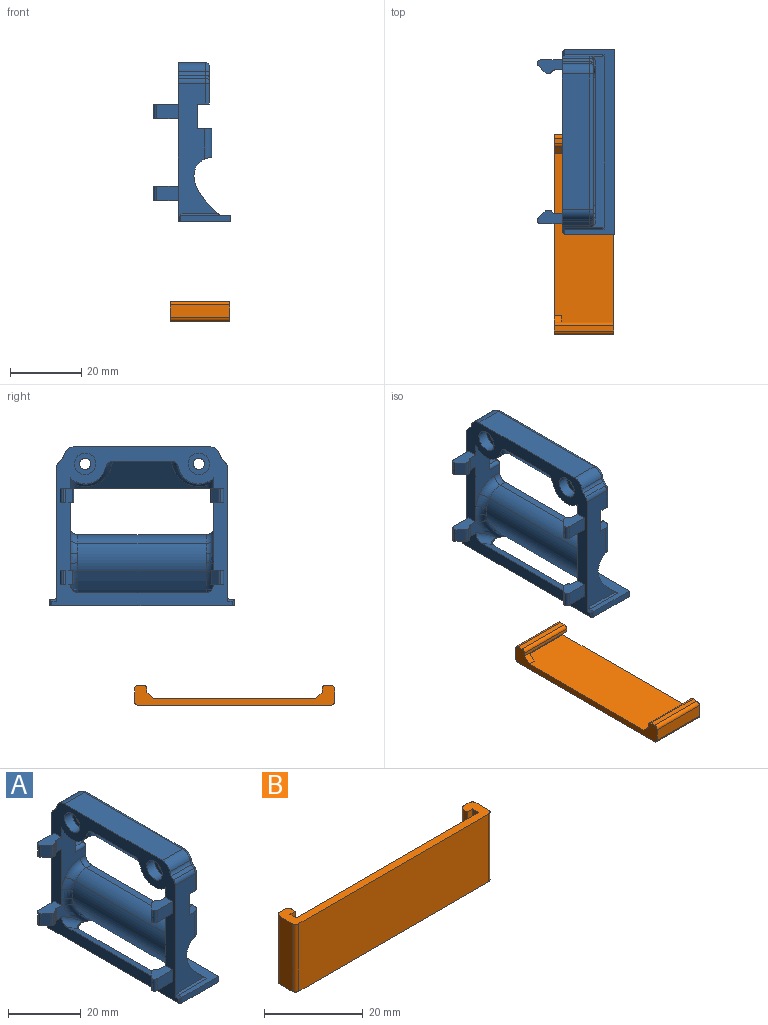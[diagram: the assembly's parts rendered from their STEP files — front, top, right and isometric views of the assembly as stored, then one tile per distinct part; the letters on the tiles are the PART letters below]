
ASSEMBLY  parts=2 mates=1
PART A: 131 faces, bbox 22.5x52.8x50.8 mm
  f0: plane 8.17x6.43mm, normal (0,1,0), area 16.5mm2, adj f30,f65,f66,f67,f90,f91,f120
  f1: plane 8.17x6.43mm, normal (0,-1,0), area 16.5mm2, adj f30,f72,f73,f74,f87,f89,f122
  f2: plane 21.12x11.5mm, normal (0,-1,0), area 100.7mm2, adj f8,f23,f28,f30,f59,f68,f69,f70
  f3: plane 21.12x11.5mm, normal (0,1,0), area 100.7mm2, adj f7,f23,f29,f30,f58,f61,f62,f63
  f4: cylinder r=1.6mm len=5.8mm, axis (-1,0,0), area 58.3mm2, adj f12,f34
  f5: cylinder r=1.6mm len=5.8mm, axis (-1,0,0), area 58.3mm2, adj f12,f36
  f6: plane 14.2x1.87mm, normal (0,-1,0), area 26.6mm2, adj f9,f17,f18,f83
  f7: plane 8.04x4.12mm, normal (1,0,0), area 26.9mm2, adj f3,f11,f22,f38,f58,f127
  f8: plane 8.04x4.12mm, normal (1,0,0), area 26.9mm2, adj f2,f11,f20,f37,f59,f129
  f9: plane 52.1x14.8mm, normal (0,0,-1), area 483.7mm2, adj f6,f16,f17,f30,f75,f76,f77,f78
  f10: cylinder r=28.2mm len=49.1mm, axis (0,1,0), area 397.8mm2, adj f18,f24,f37,f38,f85,f86
  f11: plane 48.51x3.71mm, normal (0,0,-1), area 106.9mm2, adj f7,f8,f12,f25,f37,f38,f47,f53
  f12: plane 46.1x10.6mm, normal (1,0,0), area 457.4mm2, adj f4,f5,f11,f47,f48,f49,f50,f51
  f13: plane 38.1x7.8mm, normal (0,0,1), area 297.2mm2, adj f26,f27,f30,f52
  f14: cylinder r=30mm len=36.1mm, axis (0,1,0), area 454.7mm2, adj f31,f67,f74,f78
  f15: plane 36.1x4.52mm, normal (0.53,0,0.85), area 192.5mm2, adj f30,f66,f73,f77
  f16: plane 14.2x1.87mm, normal (0,1,0), area 26.6mm2, adj f9,f17,f18,f81
  f17: plane 52.1x1.87mm, normal (1,0,0), area 97.6mm2, adj f6,f9,f16,f18
  f18: plane 52.1x14.2mm, normal (0,0,1), area 190.5mm2, adj f6,f10,f16,f17,f82,f84,f85,f86
  f19: plane 45.02x0.05mm, normal (0,0,-1), area 2.4mm2, adj f23,f32,f43,f44
  f20: plane 4x2.8mm, normal (0,0,1), area 10.3mm2, adj f8,f23,f37,f44,f59
  f21: plane 36.1x1.99mm, normal (0,0,1), area 72mm2, adj f23,f60,f61,f68
  f22: plane 4x2.8mm, normal (0,0,1), area 10.3mm2, adj f7,f23,f38,f43,f58
  f23: plane 44.1x8.12mm, normal (1,0,0), area 108.4mm2, adj f2,f3,f19,f20,f21,f22,f43,f44
  f24: cylinder r=10mm len=48.1mm, axis (0,1,0), area 243.1mm2, adj f10,f32,f37,f38
  f25: plane 36.5x7.58mm, normal (-0.74,0,-0.67), area 216.3mm2, adj f11,f30,f127,f128,f129,f130
  f26: cylinder r=3mm len=7.8mm, axis (-1,0,0), area 32.5mm2, adj f13,f30,f46,f54
  f27: cylinder r=3mm len=7.8mm, axis (1,0,0), area 32.5mm2, adj f13,f30,f45,f51
  f28: cylinder r=5.69mm len=9.7mm, axis (1,0,0), area 42.8mm2, adj f2,f30,f129,f130
  f29: cylinder r=5.69mm len=9.7mm, axis (1,0,0), area 42.8mm2, adj f3,f30,f127,f128
  f30: plane 51.59x45.49mm, normal (-1,0,0), area 651.8mm2, adj f0,f1,f2,f3,f9,f13,f15,f25
  f31: cylinder r=8mm len=36.1mm, axis (0,-1,0), area 302.4mm2, adj f14,f60,f63,f64,f65,f70,f71,f72
  f32: cylinder r=5mm len=48.1mm, axis (0,1,0), area 398mm2, adj f19,f24,f37,f38,f43,f44
  f33: cylinder r=3mm len=6mm, axis (-1,0,0), area 56.5mm2, adj f30,f34
  f34: plane 6x6mm, normal (-1,0,0), area 20.2mm2, adj f4,f33
  f35: cylinder r=3mm len=6mm, axis (-1,0,0), area 56.5mm2, adj f30,f36
  f36: plane 6x6mm, normal (-1,0,0), area 20.2mm2, adj f5,f35
  f37: plane 37.7x11.18mm, normal (0,1,0), area 245.2mm2, adj f8,f10,f11,f20,f24,f30,f32,f41
  f38: plane 37.7x11.18mm, normal (0,-1,0), area 245.2mm2, adj f7,f10,f11,f22,f24,f30,f32,f42
  f39: plane 7.8x0.91mm, normal (0,-0.71,0.71), area 10.1mm2, adj f30,f42,f45,f49
  f40: plane 7.8x0.91mm, normal (0,0.71,0.71), area 10.1mm2, adj f30,f41,f46,f57
  f41: cylinder r=2mm len=7.8mm, axis (1,0,0), area 12.3mm2, adj f30,f37,f40,f55
  f42: cylinder r=2mm len=7.8mm, axis (-1,0,0), area 12.3mm2, adj f30,f38,f39,f48
  f43: cylinder r=2mm len=8.51mm, axis (0,0,-1), area 26mm2, adj f19,f22,f23,f32,f38
  f44: cylinder r=2mm len=8.51mm, axis (0,0,-1), area 26mm2, adj f19,f20,f23,f32,f37
  f45: cylinder r=2mm len=7.8mm, axis (1,0,0), area 9.4mm2, adj f27,f30,f39,f50
  f46: cylinder r=2mm len=7.8mm, axis (-1,0,0), area 9.4mm2, adj f26,f30,f40,f56
  f47: cylinder r=1mm len=5.77mm, axis (0,0,-1), area 9.1mm2, adj f11,f12,f38,f48
  f48: torus R=1mm, axis (1,0,0), area 2mm2, adj f12,f42,f47,f49
  f49: cylinder r=1mm len=1.62mm, axis (0,-0.71,-0.71), area 2mm2, adj f12,f39,f48,f50
  f50: torus R=3mm, axis (1,0,0), area 2.2mm2, adj f12,f45,f49,f51
  f51: torus R=2mm, axis (1,0,0), area 5.7mm2, adj f12,f27,f50,f52
  f52: cylinder r=1mm len=38.1mm, axis (0,1,0), area 59.8mm2, adj f12,f13,f51,f54
  f53: cylinder r=1mm len=5.77mm, axis (0,0,-1), area 9.1mm2, adj f11,f12,f37,f55
  f54: torus R=2mm, axis (1,0,0), area 5.7mm2, adj f12,f26,f52,f56
  f55: torus R=1mm, axis (1,0,0), area 2mm2, adj f12,f41,f53,f57
  f56: torus R=3mm, axis (1,0,0), area 2.2mm2, adj f12,f46,f54,f57
  f57: cylinder r=1mm len=1.62mm, axis (0,-0.71,0.71), area 2mm2, adj f12,f40,f55,f56
  f58: cylinder r=1mm len=4mm, axis (1,0,0), area 6.3mm2, adj f3,f7,f22,f23
  f59: cylinder r=1mm len=4mm, axis (-1,0,0), area 6.3mm2, adj f2,f8,f20,f23
  f60: cylinder r=5mm len=36.1mm, axis (0,-1,0), area 183.9mm2, adj f21,f31,f62,f69
  f61: cylinder r=2.2mm len=2.2mm, axis (-1,0,0), area 6.9mm2, adj f3,f21,f23,f62
  f62: torus R=7.2mm, axis (0,-1,0), area 20.4mm2, adj f3,f60,f61,f63
  f63: torus R=10.2mm, axis (0,-1,0), area 11.8mm2, adj f3,f31,f62,f64
  f64: bspline ~4.73x2.36mm, area 9.7mm2, adj f30,f31,f63,f65
  f65: torus R=10.2mm, axis (0,-1,0), area 10mm2, adj f0,f31,f64,f67
  f66: cylinder r=2.2mm len=9.52mm, axis (-0.85,0,0.53), area 25.8mm2, adj f0,f15,f30,f67,f75
  f67: torus R=32.2mm, axis (0,-1,0), area 39.1mm2, adj f0,f14,f65,f66,f75,f76
  f68: cylinder r=2.2mm len=2.2mm, axis (1,0,0), area 6.9mm2, adj f2,f21,f23,f69
  f69: torus R=7.2mm, axis (0,-1,0), area 20.4mm2, adj f2,f60,f68,f70
  f70: torus R=10.2mm, axis (0,-1,0), area 11.8mm2, adj f2,f31,f69,f71
  f71: bspline ~4.73x2.36mm, area 9.7mm2, adj f30,f31,f70,f72
  f72: torus R=10.2mm, axis (0,-1,0), area 10mm2, adj f1,f31,f71,f74
  f73: cylinder r=2.2mm len=9.52mm, axis (0.85,0,-0.53), area 25.8mm2, adj f1,f15,f30,f74,f79
  f74: torus R=32.2mm, axis (0,-1,0), area 39.1mm2, adj f1,f14,f72,f73,f79,f80
  f75: bspline ~4.67x2.76mm, area 5mm2, adj f9,f66,f67,f76,f77
  f76: bspline ~3.88x2.85mm, area 2.1mm2, adj f9,f67,f75,f78
  f77: cylinder r=0.5mm len=36.1mm, axis (0,1,0), area 46.6mm2, adj f9,f15,f75,f79
  f78: cylinder r=0.5mm len=36.1mm, axis (0,1,0), area 11.8mm2, adj f9,f14,f76,f80
  f79: bspline ~4.67x3.16mm, area 5mm2, adj f9,f73,f74,f77,f80
  f80: bspline ~3.88x2.85mm, area 2.1mm2, adj f9,f74,f78,f79
  f81: plane 1.87x0.6mm, normal (-0.71,0.71,0), area 1.3mm2, adj f9,f16,f30,f82
  f82: plane 2x1.1mm, normal (-0.71,0,0.71), area 1.6mm2, adj f18,f30,f37,f81,f86
  f83: plane 1.87x0.6mm, normal (-0.71,-0.71,0), area 1.3mm2, adj f6,f9,f30,f84
  f84: plane 2x1.1mm, normal (-0.71,0,0.71), area 1.6mm2, adj f18,f30,f38,f83,f85
  f85: plane 11.19x0.5mm, normal (0,-0.71,0.71), area 7.5mm2, adj f10,f18,f38,f84
  f86: plane 11.19x0.5mm, normal (0,0.71,0.71), area 7.5mm2, adj f10,f18,f37,f82
  f87: plane 7x3.8mm, normal (0,0,1), area 20.4mm2, adj f1,f30,f88,f99,f106,f107,f108,f109
  f88: plane 6x4mm, normal (0,1,0), area 24mm2, adj f30,f87,f89,f107
  f89: plane 7x3.8mm, normal (0,0,-1), area 20.4mm2, adj f1,f30,f88,f99,f106,f107,f108,f109
  f90: plane 7x3.8mm, normal (0,0,1), area 20.4mm2, adj f0,f30,f92,f101,f104,f113,f114,f115
  f91: plane 7x3.8mm, normal (0,0,-1), area 20.4mm2, adj f0,f30,f92,f101,f104,f113,f114,f115
  f92: plane 6x4mm, normal (0,-1,0), area 24mm2, adj f30,f90,f91,f114
  f93: plane 7x3.8mm, normal (0,0,1), area 20.4mm2, adj f2,f30,f94,f100,f105,f110,f111,f112
  f94: plane 6x4mm, normal (0,1,0), area 24mm2, adj f30,f93,f95,f110
  f95: plane 7x3.8mm, normal (0,0,-1), area 20.4mm2, adj f2,f30,f94,f100,f105,f110,f111,f112
  f96: plane 6x4mm, normal (0,-1,0), area 24mm2, adj f30,f97,f98,f117
  f97: plane 7x3.8mm, normal (0,0,1), area 20.4mm2, adj f3,f30,f96,f102,f103,f116,f117,f118
  f98: plane 7x3.8mm, normal (0,0,-1), area 20.4mm2, adj f3,f30,f96,f102,f103,f116,f117,f118
  f99: plane 4x0.35mm, normal (0,-1,0), area 1.4mm2, adj f87,f89,f109,f126
  f100: plane 4x0.35mm, normal (0,-1,0), area 1.4mm2, adj f93,f95,f112,f125
  f101: plane 4x0.35mm, normal (0,1,0), area 1.4mm2, adj f90,f91,f113,f124
  f102: plane 4x0.35mm, normal (0,1,0), area 1.4mm2, adj f97,f98,f116,f123
  f103: plane 4x1.91mm, normal (-0.71,0.71,0), area 10.8mm2, adj f97,f98,f116,f118
  f104: plane 4x1.91mm, normal (-0.71,0.71,0), area 10.8mm2, adj f90,f91,f113,f115
  f105: plane 4x1.91mm, normal (-0.71,-0.71,0), area 10.8mm2, adj f93,f95,f111,f112
  f106: plane 4x1.91mm, normal (-0.71,-0.71,0), area 10.8mm2, adj f87,f89,f108,f109
  f107: cylinder r=1mm len=4mm, axis (0,0,1), area 6.1mm2, adj f87,f88,f89,f108
  f108: cylinder r=1mm len=4mm, axis (0,0,-1), area 2.9mm2, adj f87,f89,f106,f107
  f109: cylinder r=1mm len=4mm, axis (0,0,1), area 3.1mm2, adj f87,f89,f99,f106
  f110: cylinder r=1mm len=4mm, axis (0,0,1), area 6.1mm2, adj f93,f94,f95,f111
  f111: cylinder r=1mm len=4mm, axis (0,0,-1), area 2.9mm2, adj f93,f95,f105,f110
  f112: cylinder r=1mm len=4mm, axis (0,0,1), area 3.1mm2, adj f93,f95,f100,f105
  f113: cylinder r=1mm len=4mm, axis (0,0,-1), area 3.1mm2, adj f90,f91,f101,f104
  f114: cylinder r=1mm len=4mm, axis (0,0,-1), area 6.1mm2, adj f90,f91,f92,f115
  f115: cylinder r=1mm len=4mm, axis (0,0,1), area 2.9mm2, adj f90,f91,f104,f114
  f116: cylinder r=1mm len=4mm, axis (0,0,-1), area 3.1mm2, adj f97,f98,f102,f103
  f117: cylinder r=1mm len=4mm, axis (0,0,-1), area 6.1mm2, adj f96,f97,f98,f118
  f118: cylinder r=1mm len=4mm, axis (0,0,1), area 2.9mm2, adj f97,f98,f103,f117
  f119: cylinder r=1mm len=4mm, axis (0,0,1), area 4.2mm2, adj f3,f97,f98,f123
  f120: cylinder r=1mm len=4mm, axis (0,0,1), area 4.2mm2, adj f0,f90,f91,f124
  f121: cylinder r=1mm len=4mm, axis (0,0,1), area 4.2mm2, adj f2,f93,f95,f125
  f122: cylinder r=1mm len=4mm, axis (0,0,1), area 4.2mm2, adj f1,f87,f89,f126
  f123: cylinder r=1mm len=4mm, axis (0,0,1), area 4.2mm2, adj f97,f98,f102,f119
  f124: cylinder r=1mm len=4mm, axis (0,0,1), area 4.2mm2, adj f90,f91,f101,f120
  f125: cylinder r=1mm len=4mm, axis (0,0,1), area 4.2mm2, adj f93,f95,f100,f121
  f126: cylinder r=1mm len=4mm, axis (0,0,1), area 4.2mm2, adj f87,f89,f99,f122
  f127: cylinder r=2mm len=5.88mm, axis (0.67,0,-0.74), area 10.1mm2, adj f3,f7,f11,f25,f29,f128
  f128: bspline ~13.09x7.9mm, area 30.7mm2, adj f25,f29,f30,f127
  f129: cylinder r=2mm len=5.88mm, axis (0.67,0,-0.74), area 10.1mm2, adj f2,f8,f11,f25,f28,f130
  f130: bspline ~13.09x7.9mm, area 30.7mm2, adj f25,f28,f30,f129
PART B: 24 faces, bbox 56.3x5.6x16.8 mm
  f0: plane 56.3x5.6mm, normal (0,0,1), area 121.3mm2, adj f2,f3,f5,f6,f7,f8,f9,f10
  f1: plane 56.3x5.6mm, normal (0,0,-1), area 129.9mm2, adj f2,f5,f6,f7,f9,f13,f14,f15
  f2: plane 16.8x1.5mm, normal (0,1,0), area 25.2mm2, adj f0,f1,f20,f23
  f3: plane 14.8x1.5mm, normal (0,-1,0), area 22.2mm2, adj f0,f4,f10,f14
  f4: plane 3.3x1.8mm, normal (0,0,1), area 4.3mm2, adj f3,f9,f10,f16
  f5: plane 16.8x3.6mm, normal (-1,0,0), area 60.5mm2, adj f0,f1,f18,f23
  f6: plane 16.8x3.6mm, normal (1,0,0), area 60.5mm2, adj f0,f1,f19,f22
  f7: plane 16.8x1.5mm, normal (0,1,0), area 25.2mm2, adj f0,f1,f21,f22
  f8: plane 14.8x1.8mm, normal (1,0,0), area 26.6mm2, adj f0,f9,f11,f12
  f9: plane 52.3x16.8mm, normal (0,1,0), area 865.4mm2, adj f0,f1,f4,f8,f10,f12,f16,f17
  f10: plane 14.8x1.8mm, normal (-1,0,0), area 26.6mm2, adj f0,f3,f4,f9
  f11: plane 14.8x1.5mm, normal (0,-1,0), area 22.2mm2, adj f0,f8,f12,f13
  f12: plane 3.3x1.8mm, normal (0,0,1), area 4.3mm2, adj f8,f9,f11,f17
  f13: plane 16.8x1mm, normal (1,0,0), area 16.8mm2, adj f0,f1,f11,f17,f20
  f14: plane 16.8x1mm, normal (-1,0,0), area 16.8mm2, adj f0,f1,f3,f16,f21
  f15: plane 54.3x16.8mm, normal (0,-1,0), area 912.2mm2, adj f0,f1,f18,f19
  f16: plane 2x1.8mm, normal (-0.71,0.71,0), area 5.1mm2, adj f1,f4,f9,f14
  f17: plane 2x1.8mm, normal (0.71,0.71,0), area 5.1mm2, adj f1,f9,f12,f13
  f18: cylinder r=1mm len=16.8mm, axis (0,0,-1), area 26.4mm2, adj f0,f1,f5,f15
  f19: cylinder r=1mm len=16.8mm, axis (0,0,1), area 26.4mm2, adj f0,f1,f6,f15
  f20: cylinder r=1mm len=16.8mm, axis (0,0,1), area 26.4mm2, adj f0,f1,f2,f13
  f21: cylinder r=1mm len=16.8mm, axis (0,0,-1), area 26.4mm2, adj f0,f1,f7,f14
  f22: cylinder r=1mm len=16.8mm, axis (0,0,-1), area 26.4mm2, adj f0,f1,f6,f7
  f23: cylinder r=1mm len=16.8mm, axis (0,0,1), area 26.4mm2, adj f0,f1,f2,f5
PLACE A t=(5.69,-36.77,-9.24)mm fixed
PLACE B rot(axis=(0.58,0.58,0.58),120deg) t=(22.23,-88.97,-35.39)mm
MATE parallel B.f9 <-> A.f9  axis (0,0,1) through (13.94,-62.82,-35.39)mm
